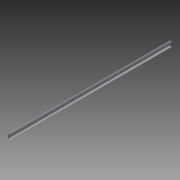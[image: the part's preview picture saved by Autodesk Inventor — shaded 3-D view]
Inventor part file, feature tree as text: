
AUTODESK INVENTOR PART (.ipt)
format: ipt  version: 2015 SP1 (Build 190203100, 203)  size: 142,336 bytes
history: native  units: in
note: dims shown in document units (in); Inventor stores cm internally (conversion verified against a paired STEP export)
features: other x3, sketch x2
ambient origin geometry x8: Origin, YZ Plane, XZ Plane, XY Plane, X Axis, Y Axis, Z Axis, Center Point
bodies: Solid1 (feature_tree)
feature tree (5):
  other  "garage door 2in rail.ipt"
  other  "Solid1::garage door 2in rail.ipt"
  other  "TaggingFeature1"
  sketch  "Sketch1"  dims[d0=0.3937in]
  sketch  "Sketch2"
